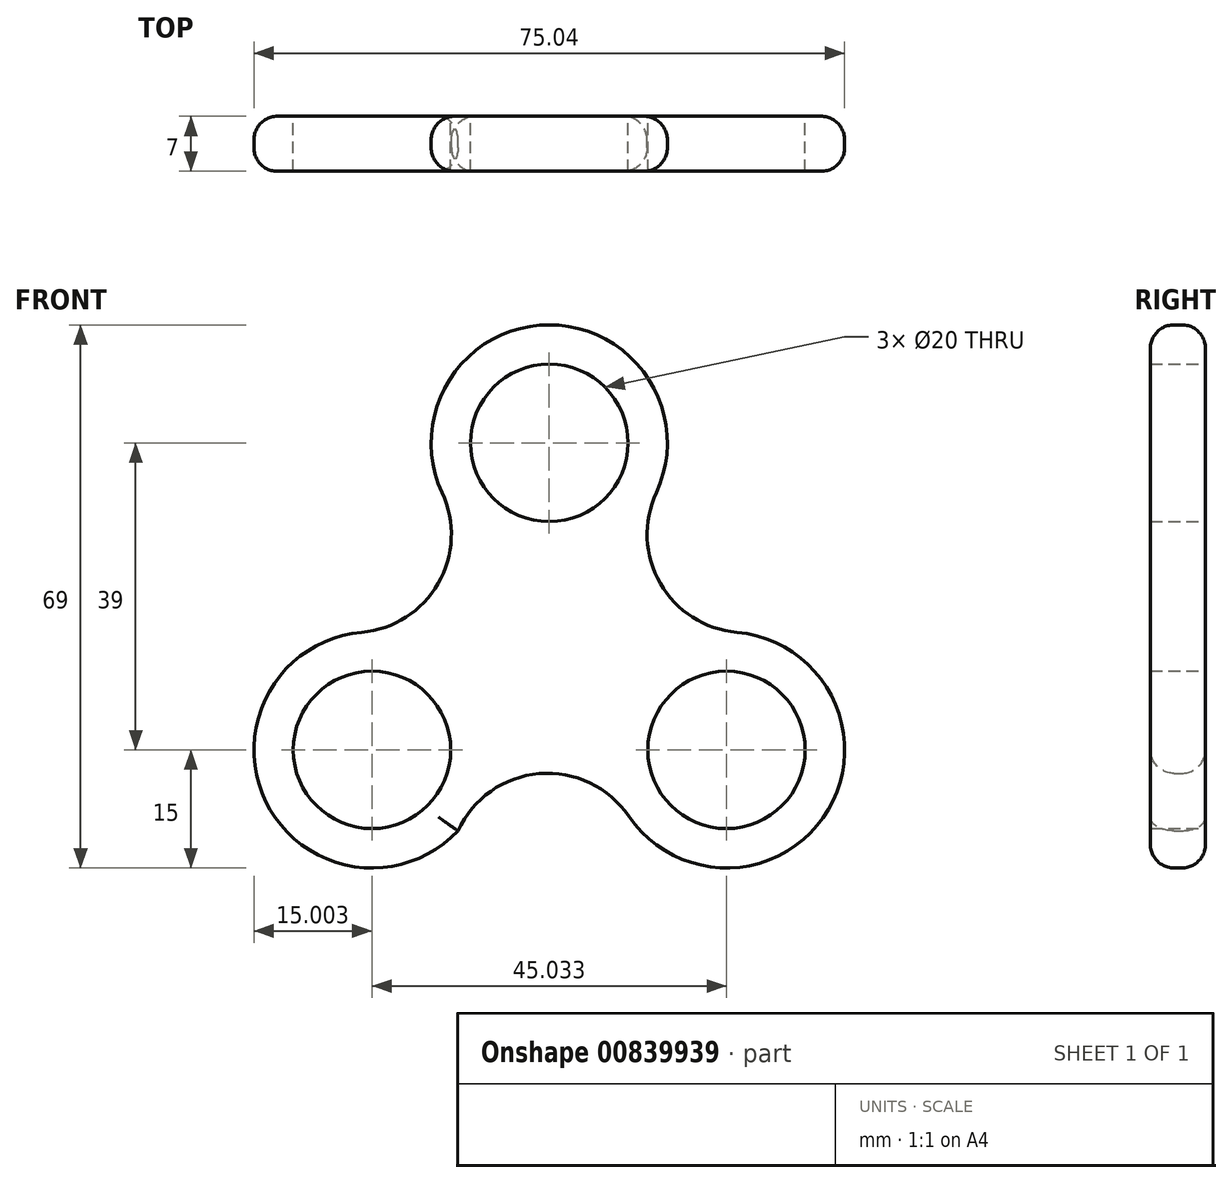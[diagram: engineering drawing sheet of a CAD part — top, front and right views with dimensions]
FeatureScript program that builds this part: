
annotation { "Feature Type Name" : "Feature", "Feature Type Description" : "" }
export const myFeature = defineFeature(function(context is Context, id is Id, definition is map)
    precondition{}
    {
        {
            var Q0;
            Q0=qCreatedBy(makeId("Front.planeOp"),FACE);
            var sketch = newSketch(context, id + "F0", { "sketchPlane" : qUnion([Q0])});
            skCircle(sketch, "E0", {"center": v(0, 0) * mm, "radius": 26 * mm, "construction": true});
            skCircle(sketch, "E1", {"center": v(0, 26) * mm, "radius": 15 * mm});
            skCircle(sketch, "E2", {"center": v(22.52, -13) * mm, "radius": 15 * mm});
            skCircle(sketch, "E3", {"center": v(-22.52, -13) * mm, "radius": 15 * mm});
            skLineSegment(sketch, "E4", {"start": v(0, 0) * mm, "end": v(-22.52, -13) * mm});
            skLineSegment(sketch, "E5", {"start": v(0, 0) * mm, "end": v(22.52, -13) * mm});
            skArc(sketch, "E6", {"start": v(-23.83, 1.94) * mm, "mid": v(-14.1, 8.14) * mm, "end": v(-13.6, 19.67) * mm});
            skArc(sketch, "E7", {"start": v(10.12, -21.44) * mm, "mid": v(-1.27, -16.01) * mm, "end": v(-11.59, -23.27) * mm});
            skArc(sketch, "E8", {"start": v(13.6, 19.67) * mm, "mid": v(14.1, 8.14) * mm, "end": v(23.83, 1.94) * mm});
            skSolve(sketch);
        }
        {
            var Q0;
            {var subQ0=sQuery(id+"F0.wireOp",EDGE,"E1");var subQ1=makeQuery(id+"F0.imprint","INTERSECT",VERTEX,{"derivedFrom":[subQ0,sQuery(id+"F0.wireOp",EDGE,"E6")]});Q0=makeQuery(id+"F0.imprint","IMPRINT",FACE,{"disambiguationData":[TD([[makeQuery(id+"F0.imprint","IMPRINT",EDGE,{"disambiguationData":[TD([[subQ1,-1.0]])],"derivedFrom":subQ0}),1.0]])]});}
            var Q1;
            {var subQ0=sQuery(id+"F0.wireOp",EDGE,"E3");var subQ1=makeQuery(id+"F0.imprint","INTERSECT",VERTEX,{"derivedFrom":[subQ0,sQuery(id+"F0.wireOp",EDGE,"E6")]});Q1=makeQuery(id+"F0.imprint","IMPRINT",FACE,{"disambiguationData":[TD([[makeQuery(id+"F0.imprint","IMPRINT",EDGE,{"disambiguationData":[TD([[subQ1,1.0]])],"derivedFrom":subQ0}),1.0]])]});}
            var Q2;
            {var subQ0=sQuery(id+"F0.wireOp",EDGE,"E2");var subQ1=makeQuery(id+"F0.imprint","INTERSECT",VERTEX,{"derivedFrom":[subQ0,sQuery(id+"F0.wireOp",EDGE,"E8")]});Q2=makeQuery(id+"F0.imprint","IMPRINT",FACE,{"disambiguationData":[TD([[makeQuery(id+"F0.imprint","IMPRINT",EDGE,{"disambiguationData":[TD([[subQ1,-1.0]])],"derivedFrom":subQ0}),1.0]])]});}
            var Q3;
            {var subQ8=sQuery(id+"F0.wireOp",EDGE,"E6");Q3=makeQuery(id+"F0.imprint","IMPRINT",FACE,{"disambiguationData":[TD([[makeQuery(id+"F0.imprint","IMPRINT",EDGE,{"derivedFrom":subQ8}),-1.0]])]});}
            var Q4;
            {var subQ3=sQuery(id+"F0.wireOp",EDGE,"E2");var subQ7=sQuery(id+"F0.wireOp",EDGE,"E7");var subQ9=makeQuery(id+"F0.imprint","INTERSECT",VERTEX,{"derivedFrom":[subQ3,subQ7]});Q4=makeQuery(id+"F0.imprint","IMPRINT",FACE,{"disambiguationData":[TD([[makeQuery(id+"F0.imprint","IMPRINT",EDGE,{"disambiguationData":[TD([[subQ9,1.0]])],"derivedFrom":subQ3}),-1.0]])]});}
            extrude(context, id + "F1", {"entities" : qUnion([Q0, Q1, Q2, Q3, Q4]), "endBound" : BoundingType.SYMMETRIC, "depth" : 7 * mm, "offsetDistance" : 25 * mm});
        }
        {
            var Q0;
            Q0=makeQuery(id+"F1.opExtrude","CAP_FACE",FACE,{"disambiguationData":[OSD([sQuery(id+"F0.wireOp",EDGE,"E1"),sQuery(id+"F0.wireOp",EDGE,"E2"),sQuery(id+"F0.wireOp",EDGE,"E3"),sQuery(id+"F0.wireOp",EDGE,"E6"),sQuery(id+"F0.wireOp",EDGE,"E7"),sQuery(id+"F0.wireOp",EDGE,"E8")])],"isStart":false});
            var Q1;
            Q1=makeQuery(id+"F1.opExtrude","CAP_FACE",FACE,{"disambiguationData":[OSD([sQuery(id+"F0.wireOp",EDGE,"E1"),sQuery(id+"F0.wireOp",EDGE,"E2"),sQuery(id+"F0.wireOp",EDGE,"E3"),sQuery(id+"F0.wireOp",EDGE,"E6"),sQuery(id+"F0.wireOp",EDGE,"E7"),sQuery(id+"F0.wireOp",EDGE,"E8")])],"isStart":true});
            fillet(context, id + "F2", {"entities" : qUnion([Q0, Q1]), "radius" : 3 * mm, "tangentPropagation" : true, "allowEdgeOverflow" : false});
        }
        {
            var Q0;
            Q0=makeQuery(id+"F1.opExtrude","CAP_FACE",FACE,{"disambiguationData":[OSD([sQuery(id+"F0.wireOp",EDGE,"E1"),sQuery(id+"F0.wireOp",EDGE,"E2"),sQuery(id+"F0.wireOp",EDGE,"E3"),sQuery(id+"F0.wireOp",EDGE,"E6"),sQuery(id+"F0.wireOp",EDGE,"E7"),sQuery(id+"F0.wireOp",EDGE,"E8")])],"isStart":true});
            var sketch = newSketch(context, id + "F3", { "sketchPlane" : qUnion([Q0])});
            skPoint(sketch, "E9", {"position": v(-22.52, -13) * mm});
            skPoint(sketch, "E10", {"position": v(0, 26) * mm});
            skPoint(sketch, "E11", {"position": v(22.52, -13) * mm});
            skSolve(sketch);
        }
        {
            var Q0;
            Q0=sQuery(id+"F3.wireOp",VERTEX,"E10");
            var Q1;
            Q1=sQuery(id+"F3.wireOp",VERTEX,"E9");
            var Q2;
            Q2=sQuery(id+"F3.wireOp",VERTEX,"E11");
            var Q3;
            Q3=makeQuery(id+"F1.opExtrude","SWEPT_BODY",BODY,{"disambiguationData":[OSD([sQuery(id+"F0.wireOp",EDGE,"E1"),sQuery(id+"F0.wireOp",EDGE,"E2"),sQuery(id+"F0.wireOp",EDGE,"E3"),sQuery(id+"F0.wireOp",EDGE,"E6"),sQuery(id+"F0.wireOp",EDGE,"E7"),sQuery(id+"F0.wireOp",EDGE,"E8")])]});
            hole(context, id + "F4", {"style" : HoleStyle.SIMPLE, "endStyle" : HoleEndStyle.THROUGH, "holeDiameter" : 20 * mm, "majorDiameter" : 5 * mm, "isTappedThrough" : true, "tappedDepth" : 12 * mm, "tapClearance" : 3, "locations" : qUnion([Q0, Q1, Q2]), "scope" : qUnion([Q3])});
        }
    });
